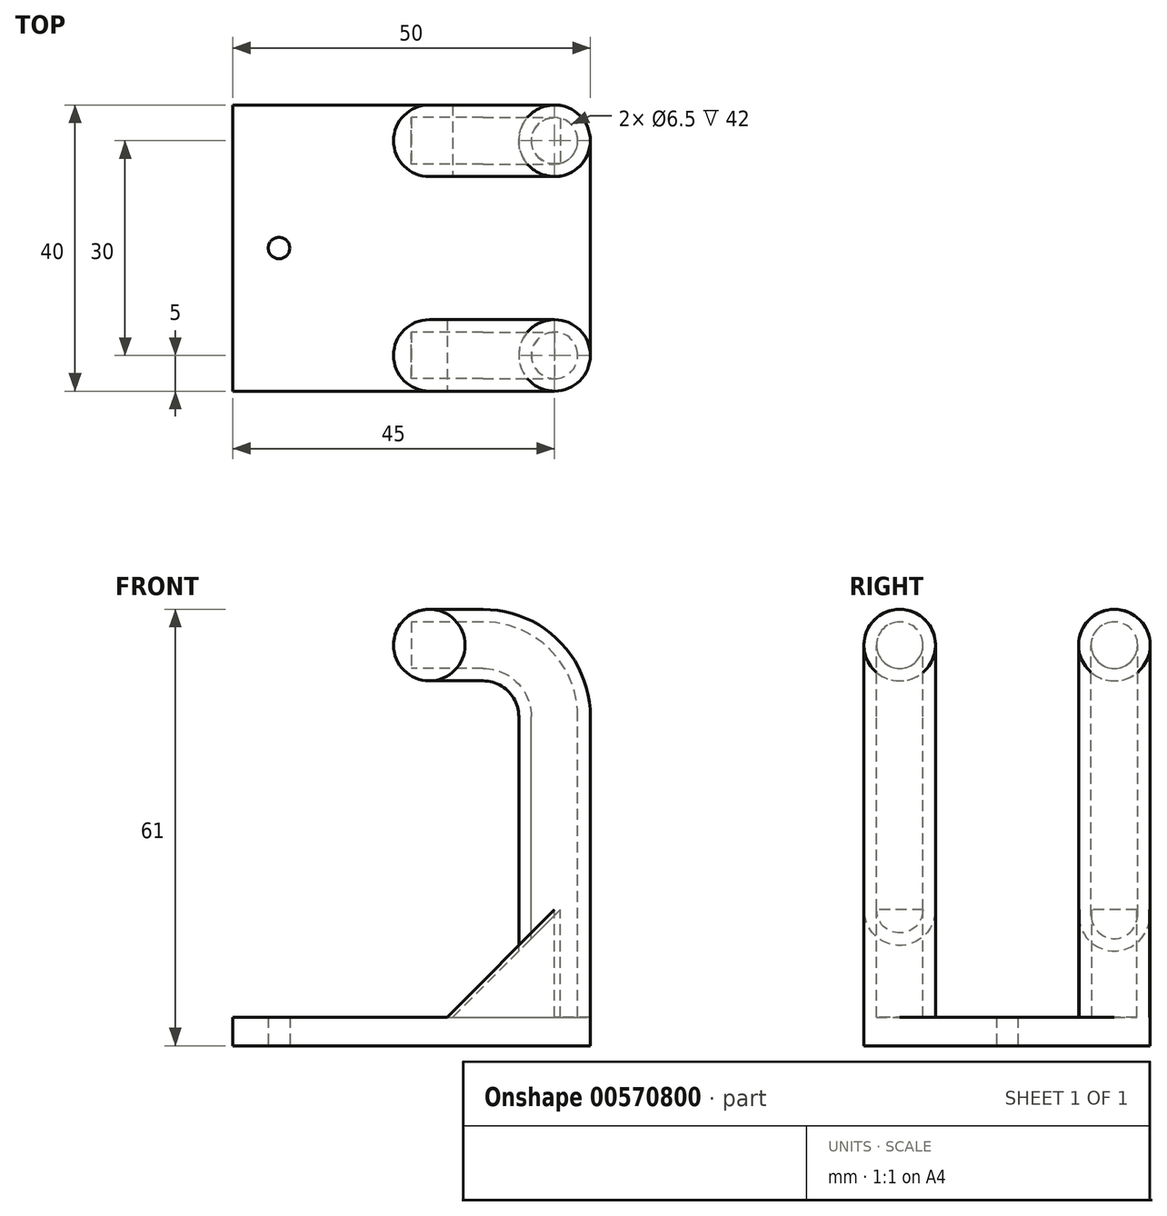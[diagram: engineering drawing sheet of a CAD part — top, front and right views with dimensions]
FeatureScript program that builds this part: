
annotation { "Feature Type Name" : "Feature", "Feature Type Description" : "" }
export const myFeature = defineFeature(function(context is Context, id is Id, definition is map)
    precondition{}
    {
        {
            var Q0;
            Q0=qCreatedBy(makeId("Top.planeOp"),FACE);
            var sketch = newSketch(context, id + "F0", { "sketchPlane" : qUnion([Q0])});
            skLineSegment(sketch, "E0.bottom", {"start": v(-25, 20) * mm, "end": v(25, 20) * mm});
            skLineSegment(sketch, "E0.top", {"start": v(-25, -20) * mm, "end": v(25, -20) * mm});
            skLineSegment(sketch, "E0.left", {"start": v(-25, 20) * mm, "end": v(-25, -20) * mm});
            skLineSegment(sketch, "E0.right", {"start": v(25, 20) * mm, "end": v(25, -20) * mm});
            skPoint(sketch, "E0.middle", {"position": v(0, 0) * mm});
            skCircle(sketch, "E1", {"center": v(-18.5, 0) * mm, "radius": 1.5 * mm});
            skSolve(sketch);
        }
        {
            var Q0;
            Q0=makeQuery(id+"F0.imprint","IMPRINT",FACE,{"disambiguationData":[TD([[makeQuery(id+"F0.imprint","IMPRINT",EDGE,{"derivedFrom":sQuery(id+"F0.wireOp",EDGE,"E0.bottom")}),-1.0]])]});
            extrude(context, id + "F1", {"entities" : qUnion([Q0]), "depth" : 4 * mm, "offsetDistance" : 25 * mm});
        }
        {
            var Q0;
            Q0=makeQuery(id+"F1.opExtrude","CAP_FACE",FACE,{"disambiguationData":[OSD([sQuery(id+"F0.wireOp",EDGE,"E0.bottom"),sQuery(id+"F0.wireOp",EDGE,"E0.top"),sQuery(id+"F0.wireOp",EDGE,"E0.left"),sQuery(id+"F0.wireOp",EDGE,"E0.right"),sQuery(id+"F0.wireOp",EDGE,"E1")])],"isStart":false});
            var sketch = newSketch(context, id + "F2", { "sketchPlane" : qUnion([Q0])});
            skCircle(sketch, "E2", {"center": v(20, -15) * mm, "radius": 5 * mm});
            skCircle(sketch, "E3", {"center": v(20, 15) * mm, "radius": 5 * mm});
            skCircle(sketch, "E4", {"center": v(20, 15) * mm, "radius": 3.25 * mm});
            skCircle(sketch, "E5", {"center": v(20, -15) * mm, "radius": 3.25 * mm});
            skSolve(sketch);
        }
        {
            var Q0;
            Q0=sQuery(id+"F2.wireOp",VERTEX,"E3.center");
            var Q1;
            Q1=makeQuery(id+"F1.opExtrude","CAP_EDGE",EDGE,{"disambiguationData":[OSD([sQuery(id+"F0.wireOp",EDGE,"E0.right")])],"isStart":false});
            cPlane(context, id + "F3", {"entities" : qUnion([Q0, Q1]), "cplaneType" : CPlaneType.LINE_POINT, "offset" : 25 * mm, "width" : 150 * mm, "height" : 150 * mm});
        }
        {
            var Q0;
            Q0=qCreatedBy(id+"F3.planeOp",FACE);
            var sketch = newSketch(context, id + "F4", { "sketchPlane" : qUnion([Q0])});
            skLineSegment(sketch, "E6", {"start": v(20, 4) * mm, "end": v(20, 46) * mm});
            skLineSegment(sketch, "E7", {"start": v(10, 56) * mm, "end": v(0, 56) * mm});
            skPoint(sketch, "E8.visualSharp", {"position": v(20, 56) * mm});
            skArc(sketch, "E8.filletArc", {"start": v(20, 46) * mm, "mid": v(17.07, 53.07) * mm, "end": v(10, 56) * mm});
            skSolve(sketch);
        }
        {
            var Q0;
            Q0=makeQuery(id+"F2.imprint","IMPRINT",FACE,{"disambiguationData":[TD([[makeQuery(id+"F2.imprint","IMPRINT",EDGE,{"derivedFrom":sQuery(id+"F2.wireOp",EDGE,"E4")}),-1.0]])]});
            var Q1;
            Q1=sQuery(id+"F4.wireOp",EDGE,"E6");
            var Q2;
            Q2=sQuery(id+"F4.wireOp",EDGE,"E8.filletArc");
            var Q3;
            Q3=sQuery(id+"F4.wireOp",EDGE,"E7");
            sweep(context, id + "F5", {"operationType" : NewBodyOperationType.ADD, "profiles" : qUnion([Q0]), "path" : qUnion([Q1, Q2, Q3])});
        }
        {
            var Q0;
            Q0=sQuery(id+"F2.wireOp",VERTEX,"E2.center");
            var Q1;
            Q1=sQuery(id+"F0.wireOp",EDGE,"E0.right");
            cPlane(context, id + "F6", {"entities" : qUnion([Q0, Q1]), "cplaneType" : CPlaneType.LINE_POINT, "offset" : 25 * mm, "width" : 150 * mm, "height" : 150 * mm});
        }
        {
            var Q0;
            Q0=qCreatedBy(id+"F6.planeOp",FACE);
            var sketch = newSketch(context, id + "F7", { "sketchPlane" : qUnion([Q0])});
            skLineSegment(sketch, "E9", {"start": v(20, 4) * mm, "end": v(20, 46) * mm});
            skLineSegment(sketch, "E10", {"start": v(10, 56) * mm, "end": v(0, 56) * mm});
            skPoint(sketch, "E11.visualSharp", {"position": v(20, 56) * mm});
            skArc(sketch, "E11.filletArc", {"start": v(20, 46) * mm, "mid": v(17.07, 53.07) * mm, "end": v(10, 56) * mm});
            skSolve(sketch);
        }
        {
            var Q0;
            Q0=makeQuery(id+"F2.imprint","IMPRINT",FACE,{"disambiguationData":[TD([[makeQuery(id+"F2.imprint","IMPRINT",EDGE,{"derivedFrom":sQuery(id+"F2.wireOp",EDGE,"E5")}),-1.0]])]});
            var Q1;
            Q1=sQuery(id+"F7.wireOp",EDGE,"E9");
            var Q2;
            Q2=sQuery(id+"F7.wireOp",EDGE,"E11.filletArc");
            var Q3;
            Q3=sQuery(id+"F7.wireOp",EDGE,"E10");
            sweep(context, id + "F8", {"operationType" : NewBodyOperationType.ADD, "profiles" : qUnion([Q0]), "path" : qUnion([Q1, Q2, Q3])});
        }
        {
            var Q0;
            Q0=makeQuery(id+"F8.opSweep","CAP_FACE",FACE,{"disambiguationData":[OSD([sQuery(id+"F2.wireOp",EDGE,"E2"),sQuery(id+"F2.wireOp",EDGE,"E5"),sQuery(id+"F7.wireOp",VERTEX,"E10.end")])],"isStart":false});
            var sketch = newSketch(context, id + "F9", { "sketchPlane" : qUnion([Q0])});
            skCircle(sketch, "E12", {"center": v(15, 56) * mm, "radius": 5 * mm});
            skSolve(sketch);
        }
        {
            var Q0;
            Q0 = qSketchRegion(id + "F9", true);
            extrude(context, id + "F10", {"entities" : qUnion([Q0]), "operationType" : NewBodyOperationType.ADD, "depth" : 2.5 * mm, "offsetDistance" : 25 * mm});
        }
        {
            var Q0;
            Q0=makeQuery(id+"F10.opExtrude","CAP_FACE",FACE,{"disambiguationData":[OSD([sQuery(id+"F9.wireOp",EDGE,"E12")])],"isStart":false});
            fillet(context, id + "F11", {"entities" : qUnion([Q0]), "radius" : 5 * mm, "tangentPropagation" : true, "allowEdgeOverflow" : false});
        }
        {
            var Q0;
            Q0=makeQuery(id+"F5.opSweep","CAP_FACE",FACE,{"disambiguationData":[OSD([sQuery(id+"F2.wireOp",EDGE,"E3"),sQuery(id+"F2.wireOp",EDGE,"E4"),sQuery(id+"F4.wireOp",VERTEX,"E7.end")])],"isStart":false});
            var sketch = newSketch(context, id + "F12", { "sketchPlane" : qUnion([Q0])});
            skCircle(sketch, "E13", {"center": v(-15, 56) * mm, "radius": 5 * mm});
            skSolve(sketch);
        }
        {
            var Q0;
            Q0 = qSketchRegion(id + "F12", true);
            extrude(context, id + "F13", {"entities" : qUnion([Q0]), "operationType" : NewBodyOperationType.ADD, "depth" : 2.5 * mm, "offsetDistance" : 25 * mm});
        }
        {
            var Q0;
            Q0=makeQuery(id+"F13.opExtrude","CAP_FACE",FACE,{"disambiguationData":[OSD([sQuery(id+"F12.wireOp",EDGE,"E13")])],"isStart":false});
            fillet(context, id + "F14", {"entities" : qUnion([Q0]), "radius" : 5 * mm, "tangentPropagation" : true, "allowEdgeOverflow" : false});
        }
        {
            var Q0;
            Q0=makeQuery(id+"F1.opExtrude","SWEPT_FACE",FACE,{"disambiguationData":[OSD([sQuery(id+"F0.wireOp",EDGE,"E0.bottom")])]});
            cPlane(context, id + "F15", {"entities" : qUnion([Q0]), "cplaneType" : CPlaneType.OFFSET, "offset" : 10 * mm, "oppositeDirection" : true, "width" : 150 * mm, "height" : 150 * mm});
        }
        {
            var Q0;
            Q0=qCreatedBy(id+"F15.planeOp",FACE);
            var sketch = newSketch(context, id + "F16", { "sketchPlane" : qUnion([Q0])});
            skLineSegment(sketch, "E14", {"start": v(-5.78, 4) * mm, "end": v(-20.78, 19) * mm});
            skLineSegment(sketch, "E15", {"start": v(-5.78, 4) * mm, "end": v(-20.78, 4) * mm});
            skLineSegment(sketch, "E16", {"start": v(-20.78, 4) * mm, "end": v(-20.78, 19) * mm});
            skSolve(sketch);
        }
        {
            var Q0;
            Q0 = qSketchRegion(id + "F16", true);
            extrude(context, id + "F17", {"entities" : qUnion([Q0]), "operationType" : NewBodyOperationType.ADD, "depth" : 10 * mm, "offsetDistance" : 25 * mm});
        }
        {
            var Q0;
            {var subQ0=sQuery(id+"F2.wireOp",EDGE,"E2");var subQ1=makeQuery(id+"F1.opExtrude","CAP_EDGE",EDGE,{"disambiguationData":[OSD([sQuery(id+"F0.wireOp",EDGE,"E0.top")])],"isStart":false});var subQ2=makeQuery(id+"F2.imprint","INTERSECT",VERTEX,{"derivedFrom":[subQ1,subQ0]});Q0=makeQuery(id+"F2.imprint","IMPRINT",FACE,{"disambiguationData":[TD([[makeQuery(id+"F2.imprint","IMPRINT",EDGE,{"disambiguationData":[TD([[subQ2,-1.0]])],"derivedFrom":subQ0}),-1.0]])]});}
            var Q1;
            {var subQ0=sQuery(id+"F2.wireOp",EDGE,"E3");var subQ1=makeQuery(id+"F1.opExtrude","CAP_EDGE",EDGE,{"disambiguationData":[OSD([sQuery(id+"F0.wireOp",EDGE,"E0.bottom")])],"isStart":false});var subQ2=makeQuery(id+"F2.imprint","INTERSECT",VERTEX,{"derivedFrom":[subQ1,subQ0]});Q1=makeQuery(id+"F2.imprint","IMPRINT",FACE,{"disambiguationData":[TD([[makeQuery(id+"F2.imprint","IMPRINT",EDGE,{"disambiguationData":[TD([[subQ2,1.0]])],"derivedFrom":subQ0}),-1.0]])]});}
            extrude(context, id + "F18", {"entities" : qUnion([Q0, Q1]), "operationType" : NewBodyOperationType.REMOVE, "oppositeDirection" : true, "depth" : 25 * mm, "offsetDistance" : 25 * mm});
        }
        {
            var Q0;
            Q0=makeQuery(id+"F1.opExtrude","SWEPT_FACE",FACE,{"disambiguationData":[OSD([sQuery(id+"F0.wireOp",EDGE,"E0.top")])]});
            var sketch = newSketch(context, id + "F19", { "sketchPlane" : qUnion([Q0])});
            skLineSegment(sketch, "E17", {"start": v(20, 4) * mm, "end": v(20, 19) * mm});
            skLineSegment(sketch, "E18", {"start": v(20, 19) * mm, "end": v(5, 4) * mm});
            skLineSegment(sketch, "E19", {"start": v(5, 4) * mm, "end": v(20, 4) * mm});
            skSolve(sketch);
        }
        {
            var Q0;
            Q0=makeQuery(id+"F19.imprint","IMPRINT",FACE,{"disambiguationData":[TD([[makeQuery(id+"F19.imprint","IMPRINT",EDGE,{"derivedFrom":sQuery(id+"F19.wireOp",EDGE,"E17")}),1.0]])]});
            extrude(context, id + "F20", {"entities" : qUnion([Q0]), "operationType" : NewBodyOperationType.ADD, "oppositeDirection" : true, "depth" : 10 * mm, "offsetDistance" : 25 * mm});
        }
    });
